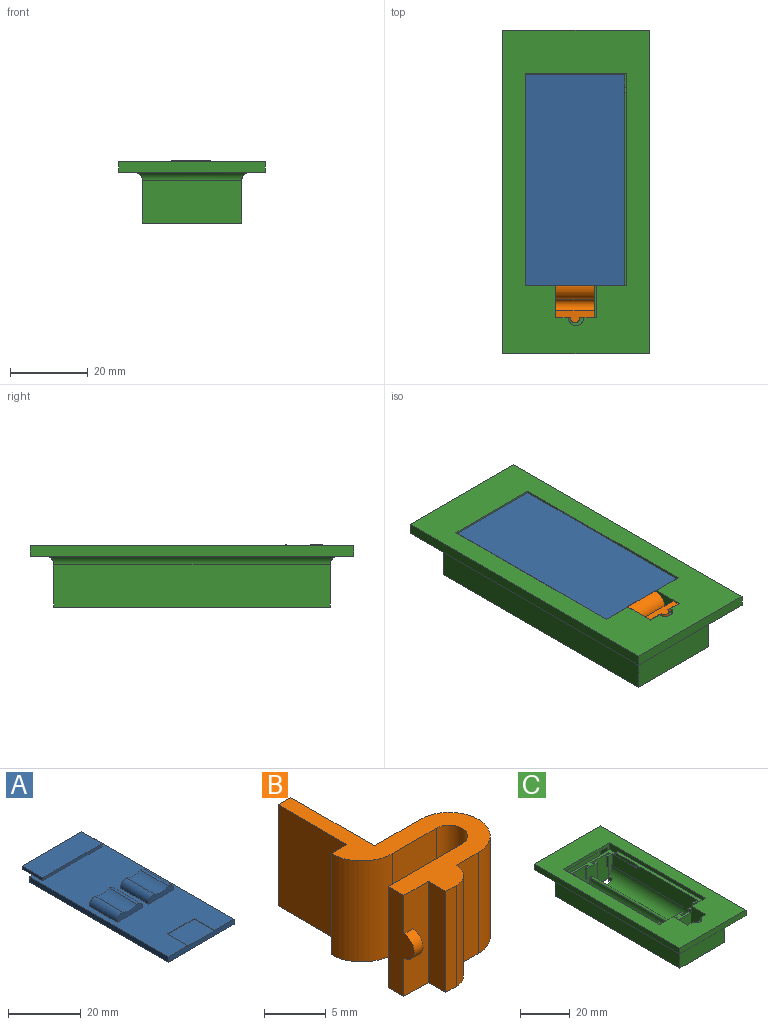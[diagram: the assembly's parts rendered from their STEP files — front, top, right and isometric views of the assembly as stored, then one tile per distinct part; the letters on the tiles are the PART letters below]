
ASSEMBLY  parts=3 mates=2
PART A: 26 faces, bbox 25.6x58.1x4.1 mm
  f0: plane 54.13x25.6mm, normal (0,0,1), area 996.4mm2, adj f1,f2,f3,f4,f6,f7,f9,f10
  f1: plane 25.6x1.8mm, normal (0,-1,0), area 44.5mm2, adj f0,f2,f4,f5,f23,f24,f25
  f2: plane 54.13x1.8mm, normal (-1,0,0), area 97.4mm2, adj f0,f1,f3,f5
  f3: plane 25.6x1.8mm, normal (0,1,0), area 46.1mm2, adj f0,f2,f4,f5,f16
  f4: plane 54.13x1.8mm, normal (1,0,0), area 97.4mm2, adj f0,f1,f3,f5
  f5: plane 54.13x25.6mm, normal (0,0,-1), area 1385.6mm2, adj f1,f2,f3,f4
  f6: cylinder r=2.2mm len=10.88mm, axis (0,1,0), area 38.8mm2, adj f0,f8,f9,f10
  f7: cylinder r=2.2mm len=10.88mm, axis (0,1,0), area 38.8mm2, adj f0,f8,f9,f10
  f8: cylinder r=5.7mm len=10.88mm, axis (0,1,0), area 62.4mm2, adj f6,f7,f9,f10
  f9: plane 9.91x2.31mm, normal (0,-1,0), area 18.1mm2, adj f0,f6,f7,f8
  f10: plane 9.91x2.31mm, normal (0,1,0), area 18.1mm2, adj f0,f6,f7,f8
  f11: cylinder r=2.2mm len=10.88mm, axis (0,1,0), area 38.8mm2, adj f0,f13,f14,f15
  f12: cylinder r=2.2mm len=10.88mm, axis (0,1,0), area 38.8mm2, adj f0,f13,f14,f15
  f13: cylinder r=5.7mm len=10.88mm, axis (0,1,0), area 62.4mm2, adj f11,f12,f14,f15
  f14: plane 9.91x2.31mm, normal (0,-1,0), area 18.1mm2, adj f0,f11,f12,f13
  f15: plane 9.91x2.31mm, normal (0,1,0), area 18.1mm2, adj f0,f11,f12,f13
  f16: plane 23.2x4mm, normal (0,0,-1), area 92.8mm2, adj f3,f17,f19,f20
  f17: plane 8x1mm, normal (-1,0,0), area 8mm2, adj f0,f16,f18,f20,f21
  f18: plane 23.2x8mm, normal (0,0,1), area 185.6mm2, adj f17,f19,f20,f21
  f19: plane 8x1mm, normal (1,0,0), area 8mm2, adj f0,f16,f18,f20,f21
  f20: plane 23.2x1mm, normal (0,1,0), area 23.2mm2, adj f16,f17,f18,f19
  f21: plane 23.2x1mm, normal (0,-1,0), area 23.2mm2, adj f0,f17,f18,f19
  f22: plane 10.3x0.15mm, normal (0,-1,0), area 1.5mm2, adj f0,f23,f24,f25
  f23: plane 7.88x0.15mm, normal (-1,0,0), area 1.2mm2, adj f0,f1,f22,f25
  f24: plane 7.88x0.15mm, normal (1,0,0), area 1.2mm2, adj f0,f1,f22,f25
  f25: plane 10.3x7.88mm, normal (0,0,1), area 81.1mm2, adj f1,f22,f23,f24
PART B: 22 faces, bbox 11.8x18.2x10 mm
  f0: plane 10x2.8mm, normal (0,-1,0), area 25.6mm2, adj f1,f2,f12,f13,f20,f21
  f1: plane 18.18x11.8mm, normal (0,0,-1), area 64mm2, adj f0,f3,f4,f5,f6,f7,f8,f9
  f2: plane 18.18x11.8mm, normal (0,0,1), area 64mm2, adj f0,f3,f4,f5,f6,f7,f8,f9
  f3: plane 10x0.01mm, normal (-1,0,0), area 0.1mm2, adj f1,f2,f4,f6
  f4: plane 10x1.8mm, normal (0,1,0), area 18mm2, adj f1,f2,f3,f17
  f5: cylinder r=1.7mm len=10mm, axis (0,0,1), area 2.5mm2, adj f1,f2,f7,f19
  f6: cylinder r=3.5mm len=10mm, axis (0,0,1), area 54.9mm2, adj f1,f2,f3,f16
  f7: plane 10x5mm, normal (0,1,0), area 50mm2, adj f1,f2,f5,f8
  f8: cylinder r=3.3mm len=10mm, axis (0,0,1), area 103.7mm2, adj f1,f2,f7,f9
  f9: plane 10x2.5mm, normal (0,-1,0), area 25mm2, adj f1,f2,f8,f10
  f10: cylinder r=2mm len=10mm, axis (0,0,1), area 31.4mm2, adj f1,f2,f9,f11
  f11: plane 10x1.2mm, normal (0,-1,0), area 12mm2, adj f1,f2,f10,f12
  f12: plane 10x2mm, normal (-1,0,0), area 20mm2, adj f0,f1,f2,f11
  f13: plane 10x3mm, normal (-1,0,0), area 20.3mm2, adj f0,f1,f2,f14,f20
  f14: plane 10x8.5mm, normal (0,1,0), area 85mm2, adj f1,f2,f13,f15
  f15: cylinder r=1.5mm len=10mm, axis (0,0,1), area 47.1mm2, adj f1,f2,f14,f16
  f16: plane 10x5mm, normal (0,-1,0), area 50mm2, adj f1,f2,f6,f15
  f17: plane 10x7.88mm, normal (-1,0,0), area 78.7mm2, adj f1,f2,f4,f18
  f18: plane 10x1.45mm, normal (0,1,0), area 14.5mm2, adj f1,f2,f17,f19
  f19: plane 10x9.56mm, normal (1,0,0), area 95.6mm2, adj f1,f2,f5,f18
  f20: cylinder r=1.2mm len=2.4mm, axis (-1,0,0), area 3.8mm2, adj f0,f13,f21
  f21: plane 2.4x1.2mm, normal (1,0,0), area 2.3mm2, adj f0,f20
PART C: 126 faces, bbox 37.6x83x15.8 mm
  f0: plane 13.65x1.4mm, normal (1,0,0), area 17.6mm2, adj f3,f99,f101,f121
  f1: plane 49.63x7.9mm, normal (0,0,1), area 81.2mm2, adj f2,f12,f19,f35,f54,f55,f56,f67
  f2: plane 13.65x1.4mm, normal (-1,0,0), area 17.6mm2, adj f1,f100,f101,f120
  f3: plane 49.63x7.9mm, normal (0,0,1), area 81.2mm2, adj f0,f19,f34,f57,f58,f68,f69,f96
  f4: plane 23.6x11.4mm, normal (0,1,0), area 269mm2, adj f5,f22,f101,f115
  f5: plane 13x4mm, normal (1,0,0), area 51.6mm2, adj f4,f6,f23,f42,f101,f115
  f6: plane 23.6x13mm, normal (0,-1,0), area 306.8mm2, adj f5,f22,f23,f115
  f7: plane 11.8x10.4mm, normal (0,-1,0), area 116.5mm2, adj f8,f13,f102,f103,f104,f106,f108,f114
  f8: plane 0.25x0.05mm, normal (0,0,-1), area 0mm2, adj f7,f103,f107,f108
  f9: plane 83.03x37.6mm, normal (0,0,-1), area 901mm2, adj f116,f117,f118,f119,f122,f123,f124,f125
  f10: plane 10.4x2mm, normal (0,0,-1), area 20.8mm2, adj f11,f106,f108,f112
  f11: plane 10.4x2.8mm, normal (0,1,0), area 24.3mm2, adj f10,f43,f106,f108,f109,f110
  f12: plane 7.85x1.8mm, normal (0,1,0), area 14.1mm2, adj f1,f43,f97,f106
  f13: plane 0.25x0.05mm, normal (0,0,-1), area 0mm2, adj f7,f102,f105,f106
  f14: plane 5x0.9mm, normal (1,0,0), area 4.5mm2, adj f15,f19,f83,f104
  f15: plane 5x1.93mm, normal (0,-1,0), area 9.6mm2, adj f14,f16,f83,f104
  f16: plane 5x0.8mm, normal (1,0,0), area 4mm2, adj f15,f20,f83,f104
  f17: plane 5x1.93mm, normal (0,-1,0), area 9.6mm2, adj f18,f21,f83,f104
  f18: plane 5x0.9mm, normal (-1,0,0), area 4.5mm2, adj f17,f19,f83,f104
  f19: plane 22.3x14mm, normal (0,1,0), area 285.2mm2, adj f1,f3,f14,f18,f50,f67,f68,f83
  f20: plane 10.23x5.95mm, normal (0,1,0), area 41.3mm2, adj f16,f21,f47,f49,f64,f80,f83,f104
  f21: plane 12.4x0.8mm, normal (-1,0,0), area 5.5mm2, adj f17,f20,f51,f59,f66,f81,f83,f104
  f22: plane 13x4mm, normal (-1,0,0), area 51.6mm2, adj f4,f6,f23,f42,f101,f115
  f23: plane 23.6x3.75mm, normal (0,0,-1), area 88.5mm2, adj f5,f6,f22,f42
  f24: plane 8.73x2.38mm, normal (0,-1,0), area 14.4mm2, adj f29,f34,f47,f90,f95,f101
  f25: plane 5.2x1.93mm, normal (0,1,0), area 10mm2, adj f26,f37,f94,f101
  f26: plane 5.2x0.9mm, normal (1,0,0), area 4.7mm2, adj f25,f38,f94,f101
  f27: plane 5.2x1.93mm, normal (0,1,0), area 10mm2, adj f28,f39,f85,f101
  f28: plane 5.2x0.8mm, normal (-1,0,0), area 4.2mm2, adj f27,f40,f85,f101
  f29: plane 5.2x0.8mm, normal (1,0,0), area 4.2mm2, adj f24,f30,f95,f101
  f30: plane 12.6x1.93mm, normal (0,1,0), area 12.2mm2, adj f29,f41,f50,f93,f95,f101
  f31: plane 5.2x0.9mm, normal (-1,0,0), area 4.7mm2, adj f32,f38,f94,f101
  f32: plane 5.2x1.93mm, normal (0,1,0), area 10mm2, adj f31,f33,f94,f101
  f33: plane 5.2x0.8mm, normal (-1,0,0), area 4.2mm2, adj f32,f36,f94,f101
  f34: plane 48.33x7.3mm, normal (1,0,0), area 333mm2, adj f3,f24,f47,f69,f99,f101
  f35: plane 48.33x7.3mm, normal (-1,0,0), area 333mm2, adj f1,f40,f49,f54,f100,f101
  f36: plane 10.43x5.95mm, normal (0,-1,0), area 42.5mm2, adj f33,f37,f47,f49,f64,f91,f94,f101
  f37: plane 12.6x0.8mm, normal (1,0,0), area 5.6mm2, adj f25,f36,f52,f53,f65,f92,f94,f101
  f38: plane 22.3x12.6mm, normal (0,-1,0), area 270.1mm2, adj f26,f31,f39,f41,f50,f94,f101
  f39: plane 12.6x1.5mm, normal (-1,0,0), area 15.8mm2, adj f27,f38,f50,f85,f87,f101
  f40: plane 10.1x2.38mm, normal (0,-1,0), area 19.4mm2, adj f28,f35,f49,f85,f86,f101
  f41: plane 12.6x0.9mm, normal (1,0,0), area 11.3mm2, adj f30,f38,f50,f101
  f42: plane 26.1x3.2mm, normal (0,-1,0), area 45.8mm2, adj f5,f22,f23,f43,f97,f98,f101
  f43: plane 83.03x37.6mm, normal (0,0,1), area 1603.9mm2, adj f11,f12,f42,f96,f97,f98,f106,f108
  f44: cylinder r=6.7mm len=48.33mm, axis (0,-1,0), area 592.1mm2, adj f45,f48,f59,f61,f65,f66,f70,f72
  f45: plane 2.87x0.78mm, normal (0,-1,0), area 1.9mm2, adj f44,f50,f70,f90
  f46: plane 2.87x0.78mm, normal (0,1,0), area 1.9mm2, adj f48,f50,f71,f78
  f47: cylinder r=5.5mm len=48.33mm, axis (0,-1,0), area 740.7mm2, adj f20,f24,f34,f36,f59,f64,f69,f72
  f48: cylinder r=6.7mm len=48.33mm, axis (0,-1,0), area 592.1mm2, adj f44,f46,f53,f60,f65,f66,f71,f77
  f49: cylinder r=5.5mm len=48.33mm, axis (0,-1,0), area 740.7mm2, adj f20,f35,f36,f40,f53,f54,f64,f77
  f50: plane 71.03x25.6mm, normal (0,0,-1), area 622.4mm2, adj f19,f30,f38,f39,f41,f45,f46,f56
  f51: plane 4.36x0.2mm, normal (0,0,-1), area 0.9mm2, adj f21,f66,f80,f81
  f52: plane 4.36x0.2mm, normal (0,0,-1), area 0.9mm2, adj f37,f65,f91,f92
  f53: plane 1.71x0.68mm, normal (0,1,0), area 0.9mm2, adj f37,f48,f49,f84
  f54: plane 10.13x2.38mm, normal (0,1,0), area 17.7mm2, adj f1,f35,f49,f55,f78,f82
  f55: plane 6.6x0.8mm, normal (-1,0,0), area 5.3mm2, adj f1,f54,f56,f82
  f56: plane 14x1.93mm, normal (0,-1,0), area 14.9mm2, adj f1,f50,f55,f67,f79,f82
  f57: plane 6.6x1.93mm, normal (0,-1,0), area 12.7mm2, adj f3,f58,f68,f73
  f58: plane 6.6x0.8mm, normal (1,0,0), area 5.3mm2, adj f3,f57,f69,f73
  f59: plane 1.71x0.68mm, normal (0,-1,0), area 0.9mm2, adj f21,f44,f47,f72
  f60: plane 2.87x1.95mm, normal (0,-1,0), area 3.5mm2, adj f48,f50,f71,f86
  f61: plane 2.87x1.95mm, normal (0,1,0), area 3.5mm2, adj f44,f50,f70,f74
  f62: plane 71.03x11mm, normal (-1,0,0), area 781.3mm2, adj f50,f111,f113,f117
  f63: plane 71.03x11mm, normal (1,0,0), area 781.3mm2, adj f50,f111,f113,f118
  f64: cylinder r=0.6mm len=48.33mm, axis (0,-1,0), area 91.1mm2, adj f20,f36,f47,f49
  f65: plane 4.36x3.93mm, normal (0,-1,0), area 9.8mm2, adj f37,f44,f48,f52,f91
  f66: plane 4.36x3.93mm, normal (0,1,0), area 9.8mm2, adj f21,f44,f48,f51,f80
  f67: plane 14x0.9mm, normal (-1,0,0), area 12.6mm2, adj f1,f19,f50,f56
  f68: plane 14x1.5mm, normal (1,0,0), area 17mm2, adj f3,f19,f50,f57,f73,f75
  f69: plane 11.5x2.38mm, normal (0,1,0), area 22.7mm2, adj f3,f34,f47,f58,f73,f74
  f70: plane 48.33x2.87mm, normal (1,0,0), area 138.9mm2, adj f44,f45,f50,f61
  f71: plane 48.33x2.87mm, normal (-1,0,0), area 138.9mm2, adj f46,f48,f50,f60
  f72: plane 2.3x1.31mm, normal (-1,0,0), area 3mm2, adj f44,f47,f59,f76
  f73: plane 1.93x0.8mm, normal (0,0,-1), area 1.2mm2, adj f57,f58,f68,f69,f74,f75
  f74: plane 7.4x2.5mm, normal (1,0,0), area 4.9mm2, adj f44,f47,f50,f61,f69,f73,f75,f76
  f75: plane 7.4x1.5mm, normal (0,-1,0), area 11.1mm2, adj f50,f68,f73,f74
  f76: plane 6x2.5mm, normal (0,-1,0), area 7.6mm2, adj f44,f47,f72,f74
  f77: plane 6.59x2.3mm, normal (0,-1,0), area 8.4mm2, adj f48,f49,f78,f80
  f78: plane 9x7.4mm, normal (-0.99,-0.16,0), area 16mm2, adj f46,f48,f49,f50,f54,f77,f79,f82
  f79: plane 7.4x0.6mm, normal (-1,0,0), area 4.4mm2, adj f50,f56,f78,f82
  f80: plane 9x7.4mm, normal (0.99,-0.16,0), area 16mm2, adj f20,f48,f49,f51,f66,f77,f81,f83
  f81: plane 7.4x4.33mm, normal (0,-1,0), area 32mm2, adj f21,f51,f80,f83
  f82: plane 1.63x0.8mm, normal (0,0,-1), area 1.3mm2, adj f54,f55,f56,f78,f79
  f83: plane 5.95x1.7mm, normal (0,0,-1), area 5.8mm2, adj f14,f15,f16,f17,f18,f19,f20,f21
  f84: plane 2.3x1.31mm, normal (1,0,0), area 3mm2, adj f48,f49,f53,f88
  f85: plane 1.93x0.8mm, normal (0,0,-1), area 1.2mm2, adj f27,f28,f39,f40,f86,f87
  f86: plane 7.4x2.5mm, normal (-1,0,0), area 4.9mm2, adj f40,f48,f49,f50,f60,f85,f87,f88
  f87: plane 7.4x1.5mm, normal (0,1,0), area 11.1mm2, adj f39,f50,f85,f86
  f88: plane 6x2.5mm, normal (0,1,0), area 7.6mm2, adj f48,f49,f84,f86
  f89: plane 6.59x2.3mm, normal (0,1,0), area 8.4mm2, adj f44,f47,f90,f91
  f90: plane 9x7.4mm, normal (0.99,0.16,0), area 16mm2, adj f24,f44,f45,f47,f50,f89,f93,f95
  f91: plane 9x7.4mm, normal (-0.99,0.16,0), area 16mm2, adj f36,f44,f47,f52,f65,f89,f92,f94
  f92: plane 7.4x4.33mm, normal (0,1,0), area 32mm2, adj f37,f52,f91,f94
  f93: plane 7.4x0.6mm, normal (1,0,0), area 4.4mm2, adj f30,f50,f90,f95
  f94: plane 5.95x1.7mm, normal (0,0,-1), area 5.8mm2, adj f25,f26,f31,f32,f33,f36,f37,f38
  f95: plane 1.63x0.8mm, normal (0,0,-1), area 1.3mm2, adj f24,f29,f30,f90,f93
  f96: plane 7.85x1.8mm, normal (0,1,0), area 14.1mm2, adj f3,f43,f98,f108
  f97: plane 54.63x3.2mm, normal (-1,0,0), area 104.9mm2, adj f1,f12,f42,f43,f101,f120
  f98: plane 54.63x3.2mm, normal (1,0,0), area 104.9mm2, adj f3,f42,f43,f96,f101,f121
  f99: plane 1.4x0.2mm, normal (0,1,0), area 0.3mm2, adj f0,f3,f34,f101
  f100: plane 1.4x0.2mm, normal (0,1,0), area 0.3mm2, adj f1,f2,f35,f101
  f101: plane 26.1x17.25mm, normal (0,0,1), area 54.9mm2, adj f0,f2,f4,f5,f22,f24,f25,f26
  f102: plane 1.6x1.45mm, normal (-1,0,0), area 2.2mm2, adj f1,f7,f13,f19,f104,f105
  f103: plane 1.6x1.45mm, normal (1,0,0), area 2.2mm2, adj f3,f7,f8,f19,f104,f107
  f104: plane 10.3x2.9mm, normal (0,0,1), area 19mm2, adj f7,f14,f15,f16,f17,f18,f19,f20
  f105: plane 1x0.05mm, normal (0,-1,0), area 0.1mm2, adj f1,f13,f102,f106
  f106: plane 14.6x10.5mm, normal (-1,0,0), area 147mm2, adj f7,f10,f11,f12,f13,f43,f105,f112
  f107: plane 1x0.05mm, normal (0,-1,0), area 0mm2, adj f3,f8,f103,f108
  f108: plane 14.6x10.5mm, normal (1,0,0), area 147mm2, adj f7,f8,f10,f11,f43,f96,f107,f112
  f109: cylinder r=2mm len=4mm, axis (0,0,1), area 7.5mm2, adj f11,f43,f110
  f110: plane 4x2mm, normal (0,0,1), area 6.3mm2, adj f11,f109
  f111: plane 25.6x11mm, normal (0,-1,0), area 281.6mm2, adj f50,f62,f63,f119
  f112: plane 11.8x10.4mm, normal (0,1,0), area 122.7mm2, adj f10,f106,f108,f114
  f113: plane 25.6x11mm, normal (0,1,0), area 281.6mm2, adj f50,f62,f63,f116
  f114: plane 10.5x10.4mm, normal (0,0,1), area 109.2mm2, adj f7,f106,f108,f112
  f115: plane 23.6x4mm, normal (0,0,1), area 94.4mm2, adj f4,f5,f6,f22
  f116: cylinder r=2mm len=29.6mm, axis (1,0,0), area 85mm2, adj f9,f113,f117,f118
  f117: cylinder r=2mm len=75.03mm, axis (0,1,0), area 227.7mm2, adj f9,f62,f116,f119
  f118: cylinder r=2mm len=75.03mm, axis (0,-1,0), area 227.7mm2, adj f9,f63,f116,f119
  f119: cylinder r=2mm len=29.6mm, axis (-1,0,0), area 85mm2, adj f9,f111,f117,f118
  f120: cylinder r=1.4mm len=1.4mm, axis (1,0,0), area 2.7mm2, adj f1,f2,f97,f101
  f121: cylinder r=1.4mm len=1.4mm, axis (1,0,0), area 2.7mm2, adj f0,f3,f98,f101
  f122: plane 83.03x2.8mm, normal (1,0,0), area 232.5mm2, adj f9,f43,f123,f125
  f123: plane 37.6x2.8mm, normal (0,-1,0), area 105.3mm2, adj f9,f43,f122,f124
  f124: plane 83.03x2.8mm, normal (-1,0,0), area 232.5mm2, adj f9,f43,f123,f125
  f125: plane 37.6x2.8mm, normal (0,1,0), area 105.3mm2, adj f9,f43,f122,f124
PLACE A rot(axis=(0,1,0),180deg) t=(-14.56,45.94,8.89)mm
PLACE B rot(axis=(0,1,0),90deg) t=(-6.26,-36.76,-36.78)mm
PLACE C t=(11.79,-35.44,-6.91)mm fixed
MATE fastened A.f0 <-> C.f3  axis (0,0,-1) through (-14.06,-23.99,7.09)mm
MATE fastened B.f17 <-> A.f25  axis (0,0,1) through (-1.26,-20.05,7.24)mm
